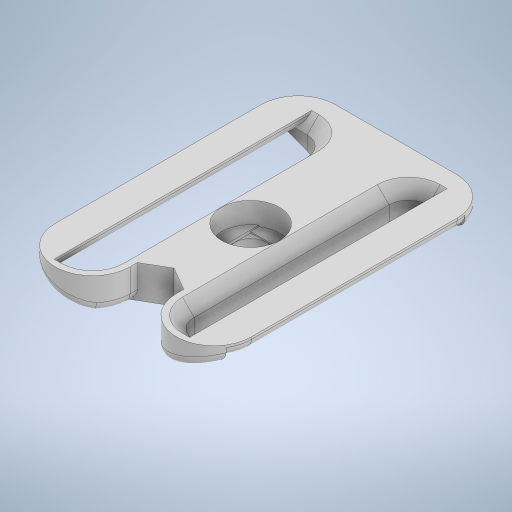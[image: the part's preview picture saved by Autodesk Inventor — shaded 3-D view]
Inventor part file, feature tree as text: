
AUTODESK INVENTOR PART (.ipt)
format: ipt  version: 2024 (Build 280153000, 153)  size: 680,448 bytes
history: native  units: in
note: dims shown in document units (in); Inventor stores cm internally (conversion verified against a paired STEP export)
features: extrude x8, chamfer x3, direct_edit x2, fillet x2, move_body x2, sketch x1
ambient origin geometry x8: Origin, YZ Plane, XZ Plane, XY Plane, X Axis, Y Axis, Z Axis, Center Point
bodies: Solid1 (feature_tree)
feature tree (18):
  sketch  "Sketch1"  dims[d2=0.1181in d3=0.0in d5=0.2677in d6=2.2146in d7=0.785in d8=0.4862in d20=0.1575in d21=0.1575in d27=0.1969in d30=0.1575in d31=0.0in d37=0.3051in d38=0.3051in d44=0.0in d45=0.0in d46=0.0in d47=0.0in d48=-0.0591in d49=0.0591in d50=0.0in d51=0.0in d52=0.0in d53=0.0in d54=-0.0197in d56=0.0591in d57=0.0118in d58=0.0in d59=0.0236in d60=0.0in d61=0.0984in d62=0.0787in d63=45.0deg d64=0.0787in d65=0.2126in d67=0.1181in d68=0.3543in d69=0.0in d73=0.0492in d74=0.0787in d75=45.0deg d76=0.0787in d79=0.0394in d86=0.1181in d87=0.0591in d88=0.0in d89=0.0591in d90=0.0787in d91=45.0deg d92=0.689in d93=0.1654in d97=0.9843in d99=0.315in d26=0.0197in d28=0.0197in d29=0.0344in d41=0.0197in d42=0.0344in d43=0.0197in d70=0.0197in d71=0.0344in]
  extrude  "Extrusion1"  Depth=0.0787in
  extrude  "Extrusion5"  Depth=0.0787in
  extrude  "Extrusion7"  Depth=0.0787in
  direct_edit  "Direct Edit2"
  extrude  "Extrusion8"  Depth=0.0787in
  direct_edit  "Direct Edit3"
  extrude  "Extrusion9"  Depth=0.0787in
  extrude  "Extrusion10"  Depth=0.0787in
  chamfer  "Chamfer2"  Distance=0.1969in
  fillet  "Fillet1"  Radius=0.1575in
  extrude  "Extrusion11"  Depth=0.0787in
  chamfer  "Chamfer4"  Distance=0.3051in
  fillet  "Fillet2"  [1 undecoded]
  extrude  "Extrusion13"  TaperAngle=0.0deg  [1 undecoded]
  chamfer  "Chamfer5"  Distance=0.0591in
  move_body  "Move2"
  move_body  "Move3"
note: 2 required parameter values undecoded (feature->parameter linkage not recoverable at this tier; creation-order binding heuristic only, values carry confidence <= 0.55)
